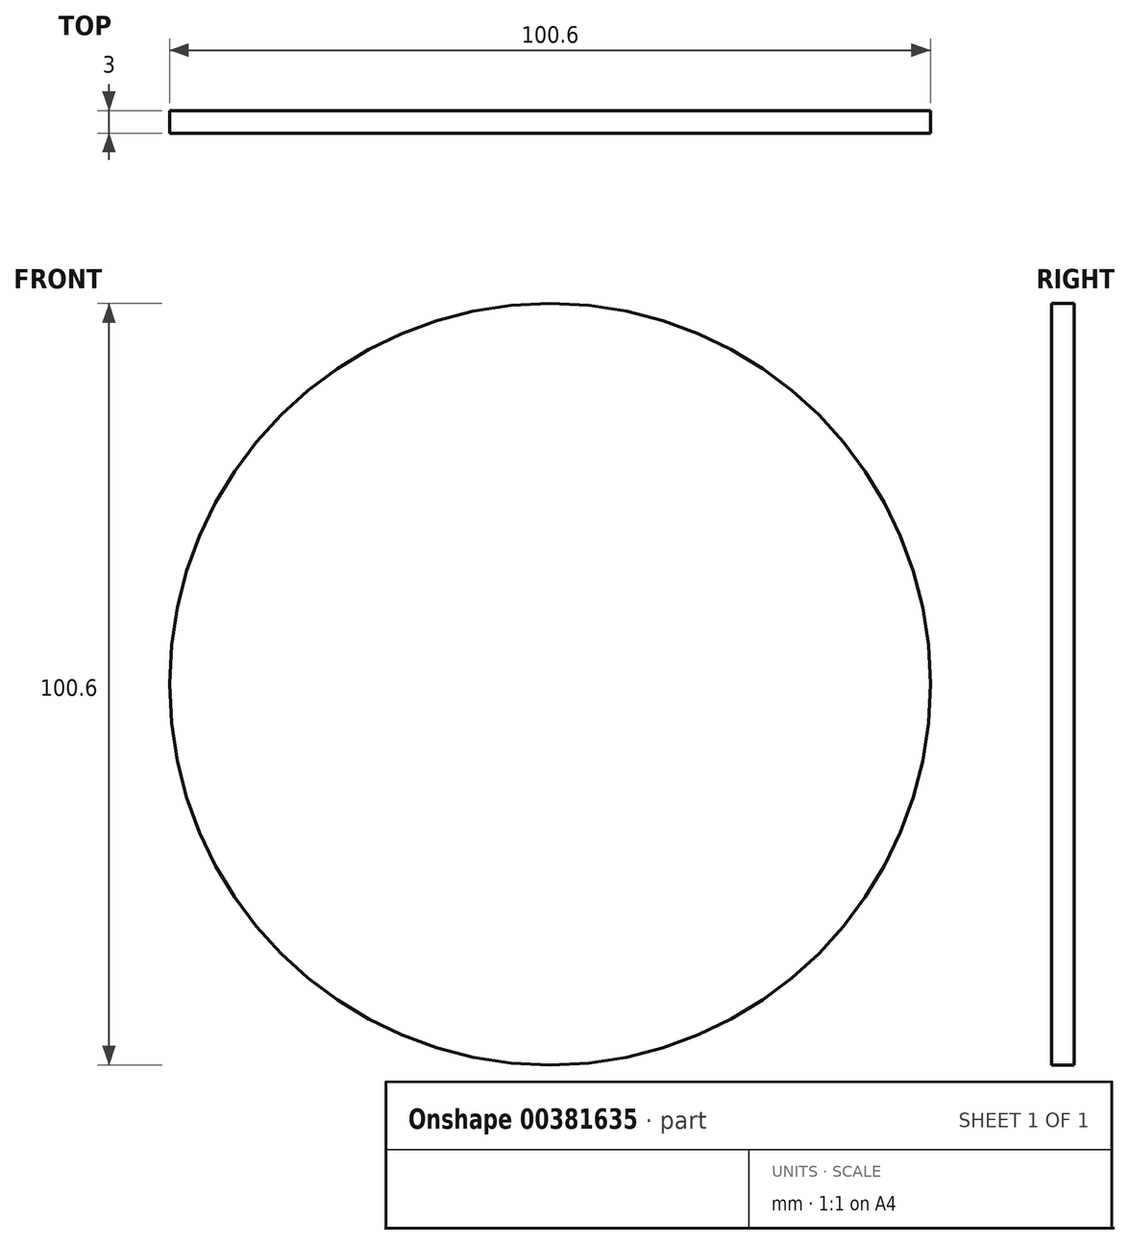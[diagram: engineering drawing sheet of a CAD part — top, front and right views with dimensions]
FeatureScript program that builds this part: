
annotation { "Feature Type Name" : "Feature", "Feature Type Description" : "" }
export const myFeature = defineFeature(function(context is Context, id is Id, definition is map)
    precondition{}
    {
        {
            var Q0;
            Q0=qCreatedBy(makeId("Front.planeOp"),FACE);
            var sketch = newSketch(context, id + "F0", { "sketchPlane" : qUnion([Q0])});
            skCircle(sketch, "E0", {"center": v(0, 0) * mm, "radius": 50.3 * mm});
            skSolve(sketch);
        }
        {
            var Q0;
            Q0 = qSketchRegion(id + "F0", true);
            extrude(context, id + "F1", {"entities" : qUnion([Q0]), "depth" : 3 * mm});
        }
    });
